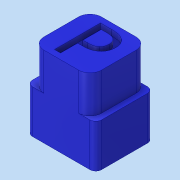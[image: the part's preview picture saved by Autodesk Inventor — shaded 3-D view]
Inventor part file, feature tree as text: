
AUTODESK INVENTOR PART (.ipt)
format: ipt  version: 2018 (Build 220112000, 112)  size: 194,048 bytes
history: native  units: mm
features: sketch x3, extrude x2, fillet x2, other x1, projected_geometry x1
ambient origin geometry x8: Origin, YZ Plane, XZ Plane, XY Plane, X Axis, Y Axis, Z Axis, Center Point
bodies: Volumenkörper1 (feature_tree)
feature tree (9):
  extrude  "Extrusion1"  Depth=10.0mm
  extrude  "Extrusion2"  Depth=10.0mm
  fillet  "Rundung1"  Radius=10.0mm
  fillet  "Rundung2"  Radius=6.5mm
  other  "Prägen1"
  sketch  "Skizze1"  dims[d0=12.0mm d1=10.0mm]
  sketch  "Skizze2"  dims[d2=14.0mm d3=0.0mm d4=10.0mm d5=10.0mm d6=6.5mm d7=0.0mm]
  sketch  "Skizze3"  dims[d8=2.0mm d9=1.0mm d10=1.0mm d11=1.0mm d12=1.0mm d13=3.490659mm]
  projected_geometry  "Projizierte Kontur1"
